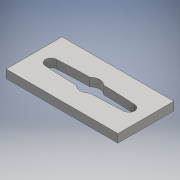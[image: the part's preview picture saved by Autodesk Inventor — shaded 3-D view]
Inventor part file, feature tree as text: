
AUTODESK INVENTOR PART (.ipt)
format: ipt  version: 2016 (Build 200138000, 138)  size: 108,032 bytes
history: native  units: mm
features: other x1, extrude x1, sketch x1
ambient origin geometry x8: Origin, YZ Plane, XZ Plane, XY Plane, X Axis, Y Axis, Z Axis, Center Point
bodies: Body1 (feature_tree)
feature tree (3):
  other  "Sólido1"
  extrude  "Extrusión1"  Depth=3.0mm TaperAngle=0.0deg
  sketch  "Boceto1"  dims[d2=40.0mm d3=3.0mm d4=0.0mm]
